# Revit family: CONV_Flokk_OffcChrs_RBMNoor6070
name_source: partatom
category: Furniture
revit_build: Autodesk Revit 2015 (Build: 20140606_1530(x64)
units: mm (PartAtom-declared; Revit-internal decimal feet)

## types (1)
- CONV_Flokk_OffcChrs_RBMNoor6070
    AssetType = Movable
    BIMObjectName = CONV_Flokk_OffcChrs_RBMNoor6070
    Brand = RBM
    Category = Office chair
    Collection = RBM Noor
    Color = Various
    ConvergoRefNr = 0119-1802-0037-NO
    Cost = 0 $
    Designer = StokkeAustad, Form Us With Love, Susanne Gronlund, Scandinavian Business Seating
    DurationUnit = Year
    ExpiringDate = 08/2018
    Features = Armrests, modular structure, adjustable seat height
armrests (optional extra), armrest height, armrest width,
seat height, seat depth, lumbar support, tilt resistance/HÅG
inBalance™, lockable tilt and foot support
    Finish = Polished aluminum
    HighestSeatingHeight = 490 mm  [stored 1.60761 ft]
    IfcExportAs = IfcFurnishingElementType
    IfcExportType = CHAIR
    LowestSeatingHeight = 355 mm
    MainColor = Various
    Manufacturer = Flokk
    ManufacturerName = Flokk
    ManufacturerURL = https://www.flokk.com
    Material = Polypropylene, metal
    Model = RBM Noor 6070
    ModelNumber = 6070
    NBSDescription = Office chairs
    NBSReference = 45-35-20/330
    Name = OffcChrs_RBMNoor6070
    NominalDepth = 605 mm  [stored 1.98491 ft]
    NominalHeight = 0 mm  [stored 0 ft]
    NominalLength = 623 mm  [stored 2.04396 ft]
    OfficeChairTertiaryMaterial = Plastic, Opaque Black
    ProductInformation = RBM Noor footbase is a brilliant chair for those who thrive in a fast-paced, creative working place and need more mobility. It comes with a five-star foot base on castors, and the seat height is adjustable. A wide range of colours are available for the polypropylene shell, which you can mix-and-match with seat cover and footbase in black, white or polished aluminium. Armrests are optional. RBM 6070 fits perfectly well in environments like open offices, project or meeting areas or homes.
    SeatingHeight = 437 mm  [stored 1.43373 ft]
    Shape = Sculptured
    Size = 665x665x727/857 mm
    URL = https://www.flokk.com
    Uniclass2 = Pr_40_50_12_57
    Uniclass2015Description = Office chairs
    Uniclass2015Reference = Pr_40_50_12_57
    Version = 1
    VersionDate = 13/03/2018
    WarrantyDurationUnit = Year
    Weight = 8.5 kg

note: [stored X ft] marks values corroborated as IEEE doubles in the binary element streams (Revit-internal decimal feet)

## geometry (parser evidence)
native form markers: Blend x8, Sweep x13
no freeform markers — native parametric forms only
